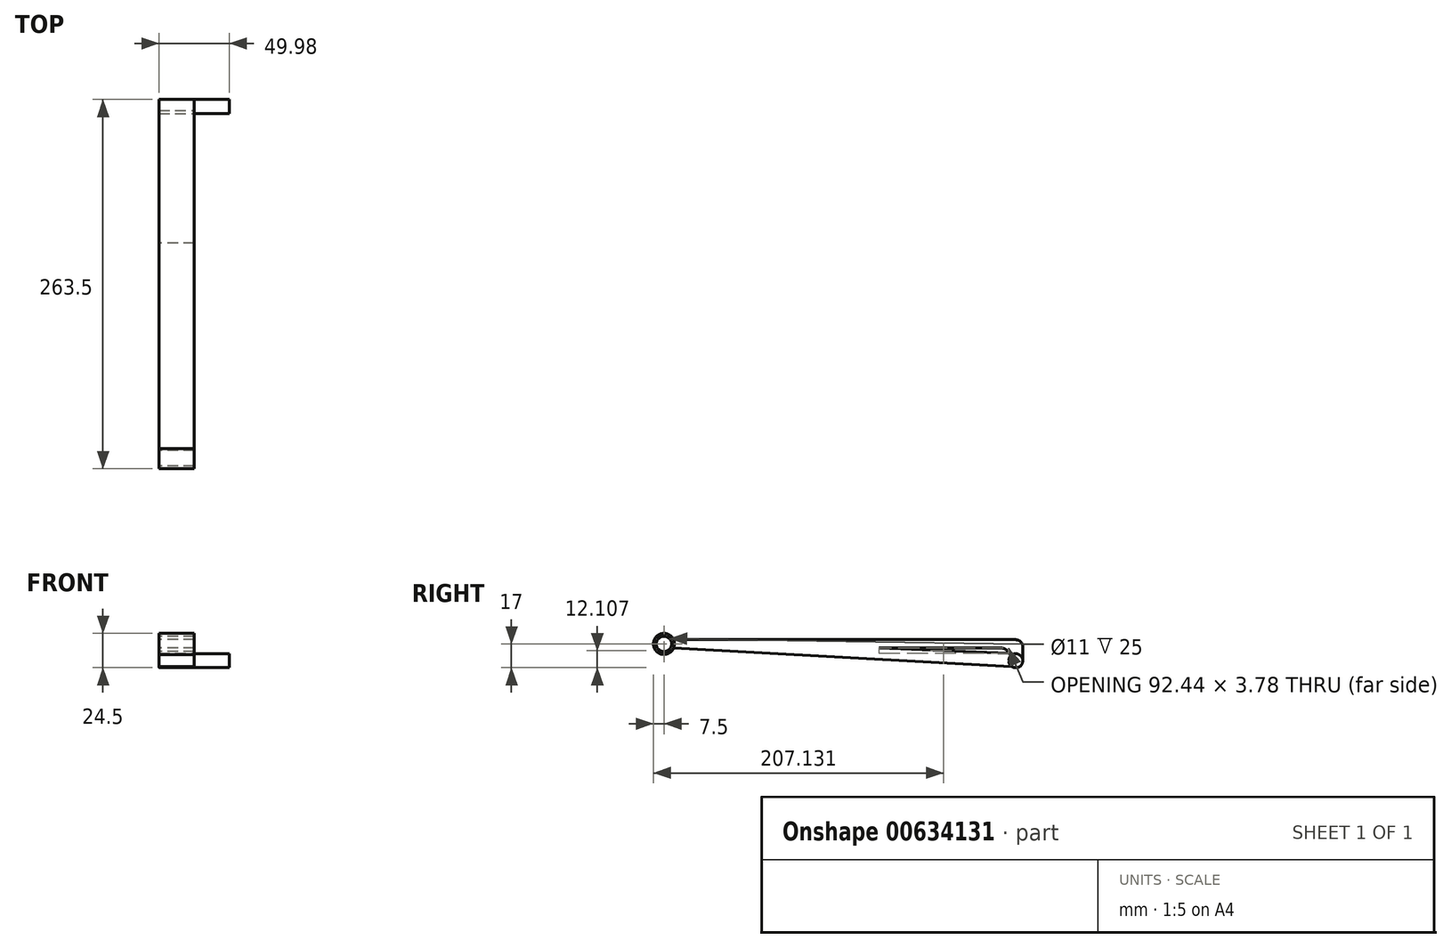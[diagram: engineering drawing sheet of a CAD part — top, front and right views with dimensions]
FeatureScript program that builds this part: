
annotation { "Feature Type Name" : "Feature", "Feature Type Description" : "" }
export const myFeature = defineFeature(function(context is Context, id is Id, definition is map)
    precondition{}
    {
        {
            var Q0;
            Q0=qCreatedBy(makeId("Right.planeOp"),FACE);
            var sketch = newSketch(context, id + "F0", { "sketchPlane" : qUnion([Q0])});
            skCircle(sketch, "E0", {"center": v(0, 0) * mm, "radius": 5 * mm, "construction": true});
            skCircle(sketch, "E1.0", {"center": v(0, 0) * mm, "radius": 5.5 * mm});
            skCircle(sketch, "E2.0", {"center": v(0, 0) * mm, "radius": 7.5 * mm});
            skSolve(sketch);
        }
        {
            var Q0;
            Q0 = qSketchRegion(id + "F0", true);
            extrude(context, id + "F1", {"entities" : qUnion([Q0]), "depth" : 25 * mm, "offsetDistance" : 25 * mm});
        }
        {
            var Q0;
            Q0=qCreatedBy(makeId("Front.planeOp"),FACE);
            cPlane(context, id + "F2", {"entities" : qUnion([Q0]), "cplaneType" : CPlaneType.OFFSET, "offset" : 6 * mm, "oppositeDirection" : true, "width" : 150 * mm, "height" : 150 * mm});
        }
        {
            var Q0;
            Q0=qCreatedBy(id+"F2.planeOp",FACE);
            var sketch = newSketch(context, id + "F3", { "sketchPlane" : qUnion([Q0])});
            skLineSegment(sketch, "E3", {"start": v(0, 0) * mm, "end": v(24.98, 0) * mm, "construction": true});
            skLineSegment(sketch, "E4", {"start": v(0, 3) * mm, "end": v(0, -3) * mm});
            skLineSegment(sketch, "E5", {"start": v(24.98, 3) * mm, "end": v(24.98, -3) * mm});
            skLineSegment(sketch, "E6", {"start": v(24.98, 3) * mm, "end": v(0, 3) * mm});
            skLineSegment(sketch, "E7", {"start": v(0, -3) * mm, "end": v(24.98, -3) * mm});
            skSolve(sketch);
        }
        {
            var Q0;
            Q0 = qSketchRegion(id + "F3", true);
            extrude(context, id + "F4", {"entities" : qUnion([Q0]), "operationType" : NewBodyOperationType.ADD, "oppositeDirection" : true, "depth" : 250 * mm, "offsetDistance" : 25 * mm});
        }
        {
            var Q0;
            Q0=makeQuery(id+"F4.opExtrude","SWEPT_FACE",FACE,{"disambiguationData":[OSD([sQuery(id+"F3.wireOp",EDGE,"E5")])]});
            var sketch = newSketch(context, id + "F5", { "sketchPlane" : qUnion([Q0])});
            skLineSegment(sketch, "E8", {"start": v(256, 3) * mm, "end": v(256, -17) * mm});
            skLineSegment(sketch, "E9", {"start": v(256, -17) * mm, "end": v(246, -17) * mm});
            skLineSegment(sketch, "E10", {"start": v(246, -17) * mm, "end": v(246, 3) * mm});
            skLineSegment(sketch, "E11", {"start": v(246, 3) * mm, "end": v(256, 3) * mm});
            skSolve(sketch);
        }
        {
            var Q0;
            Q0 = qSketchRegion(id + "F5", true);
            var Q1;
            Q1=makeQuery(id+"F4.boolean.opBoolean","MERGE",FACE,{"derivedFrom":[makeQuery(id+"F1.opExtrude","CAP_FACE",FACE,{"disambiguationData":[OSD([sQuery(id+"F0.wireOp",EDGE,"E1.0"),sQuery(id+"F0.wireOp",EDGE,"E2.0")])],"isStart":true}),makeQuery(id+"F4.opExtrude","SWEPT_FACE",FACE,{"disambiguationData":[OSD([sQuery(id+"F3.wireOp",EDGE,"E4")])]})]});
            extrude(context, id + "F6", {"entities" : qUnion([Q0]), "operationType" : NewBodyOperationType.ADD, "endBound" : BoundingType.UP_TO_SURFACE, "oppositeDirection" : true, "depth" : 25 * mm, "endBoundEntityFace" : qUnion([Q1]), "offsetDistance" : 25 * mm});
        }
        {
            var Q0;
            Q0=makeQuery(id+"F4.opExtrude","CAP_EDGE",EDGE,{"disambiguationData":[OSD([sQuery(id+"F3.wireOp",EDGE,"E6")])],"isStart":false});
            var Q1;
            Q1=makeQuery(id+"F6.boolean.opBoolean","INTERSECT",EDGE,{"derivedFrom":[makeQuery(id+"F4.opExtrude","SWEPT_FACE",FACE,{"disambiguationData":[OSD([sQuery(id+"F3.wireOp",EDGE,"E7")])]}),makeQuery(id+"F6.opExtrude","SWEPT_FACE",FACE,{"disambiguationData":[OSD([sQuery(id+"F5.wireOp",EDGE,"E10")])]})]});
            fillet(context, id + "F7", {"entities" : qUnion([Q0, Q1]), "radius" : 5 * mm, "tangentPropagation" : true, "allowEdgeOverflow" : false});
        }
        {
            var Q0;
            Q0=makeQuery(id+"F6.opExtrude","SWEPT_EDGE",EDGE,{"disambiguationData":[OSD([sQuery(id+"F5.wireOp",EDGE,"E9"),sQuery(id+"F5.wireOp",EDGE,"E10")])]});
            var Q1;
            Q1=makeQuery(id+"F6.opExtrude","SWEPT_EDGE",EDGE,{"disambiguationData":[OSD([sQuery(id+"F5.wireOp",EDGE,"E8"),sQuery(id+"F5.wireOp",EDGE,"E9")])]});
            fillet(context, id + "F8", {"entities" : qUnion([Q0, Q1]), "radius" : 5 * mm, "tangentPropagation" : true, "allowEdgeOverflow" : false});
        }
        {
            var Q0;
            Q0=makeQuery(id+"F6.boolean.opBoolean","MERGE",FACE,{"derivedFrom":[makeQuery(id+"F4.opExtrude","SWEPT_FACE",FACE,{"disambiguationData":[OSD([sQuery(id+"F3.wireOp",EDGE,"E5")])]}),makeQuery(id+"F6.opExtrude","CAP_FACE",FACE,{"disambiguationData":[OSD([sQuery(id+"F5.wireOp",EDGE,"E8"),sQuery(id+"F5.wireOp",EDGE,"E9"),sQuery(id+"F5.wireOp",EDGE,"E10"),sQuery(id+"F5.wireOp",EDGE,"E11")])],"isStart":true})]});
            var sketch = newSketch(context, id + "F9", { "sketchPlane" : qUnion([Q0])});
            skArc(sketch, "E12.0", {"start": v(246, -12) * mm, "mid": v(251, -17) * mm, "end": v(256, -12) * mm});
            skLineSegment(sketch, "E13", {"start": v(246, -12) * mm, "end": v(256, -12) * mm, "construction": true});
            skArc(sketch, "E14.MirrorCS", {"start": v(246, -12) * mm, "mid": v(251, -7) * mm, "end": v(256, -12) * mm});
            skSolve(sketch);
        }
        {
            var Q0;
            Q0=makeQuery(id+"F9.imprint","IMPRINT",FACE,{"disambiguationData":[TD([[makeQuery(id+"F9.imprint","IMPRINT",EDGE,{"derivedFrom":sQuery(id+"F9.wireOp",EDGE,"E12.0")}),1.0]])]});
            extrude(context, id + "F10", {"entities" : qUnion([Q0]), "operationType" : NewBodyOperationType.ADD, "depth" : 25 * mm, "offsetDistance" : 25 * mm});
        }
        {
            var Q0;
            Q0=makeQuery(id+"F6.boolean.opBoolean","MERGE",FACE,{"derivedFrom":[makeQuery(id+"F4.opExtrude","SWEPT_FACE",FACE,{"disambiguationData":[OSD([sQuery(id+"F3.wireOp",EDGE,"E5")])]}),makeQuery(id+"F6.opExtrude","CAP_FACE",FACE,{"disambiguationData":[OSD([sQuery(id+"F5.wireOp",EDGE,"E8"),sQuery(id+"F5.wireOp",EDGE,"E9"),sQuery(id+"F5.wireOp",EDGE,"E10"),sQuery(id+"F5.wireOp",EDGE,"E11")])],"isStart":true})]});
            var sketch = newSketch(context, id + "F11", { "sketchPlane" : qUnion([Q0])});
            skLineSegment(sketch, "E15", {"start": v(248.25, -16.1) * mm, "end": v(6.87, -3) * mm});
            skLineSegment(sketch, "E16", {"start": v(6.87, -3) * mm, "end": v(6.87, 3) * mm});
            skLineSegment(sketch, "E17", {"start": v(6.87, 3) * mm, "end": v(251, -7) * mm});
            skPoint(sketch, "E17.endSnap0", {"position": v(251, -7) * mm});
            skLineSegment(sketch, "E18", {"start": v(251, -7) * mm, "end": v(248.25, -16.1) * mm});
            skSolve(sketch);
        }
        {
            var Q0;
            Q0 = qSketchRegion(id + "F11", true);
            var Q1;
            {var subQ0=sQuery(id+"F3.wireOp",EDGE,"E4");var subQ1=sQuery(id+"F0.wireOp",EDGE,"E2.0");var subQ2=sQuery(id+"F0.wireOp",EDGE,"E1.0");Q1=makeQuery(id+"F6.boolean.opBoolean","MERGE",FACE,{"derivedFrom":[makeQuery(id+"F4.boolean.opBoolean","MERGE",FACE,{"derivedFrom":[makeQuery(id+"F1.opExtrude","CAP_FACE",FACE,{"disambiguationData":[OSD([subQ2,subQ1])],"isStart":true}),makeQuery(id+"F4.opExtrude","SWEPT_FACE",FACE,{"disambiguationData":[OSD([subQ0])]})]}),makeQuery(id+"F6.opExtrude","CAP_FACE",FACE,{"disambiguationData":[OSD([subQ2,subQ1,subQ0])],"isStart":false})]});}
            extrude(context, id + "F12", {"entities" : qUnion([Q0]), "operationType" : NewBodyOperationType.ADD, "endBound" : BoundingType.UP_TO_SURFACE, "oppositeDirection" : true, "depth" : 25 * mm, "endBoundEntityFace" : qUnion([Q1]), "offsetDistance" : 25 * mm});
        }
    });
